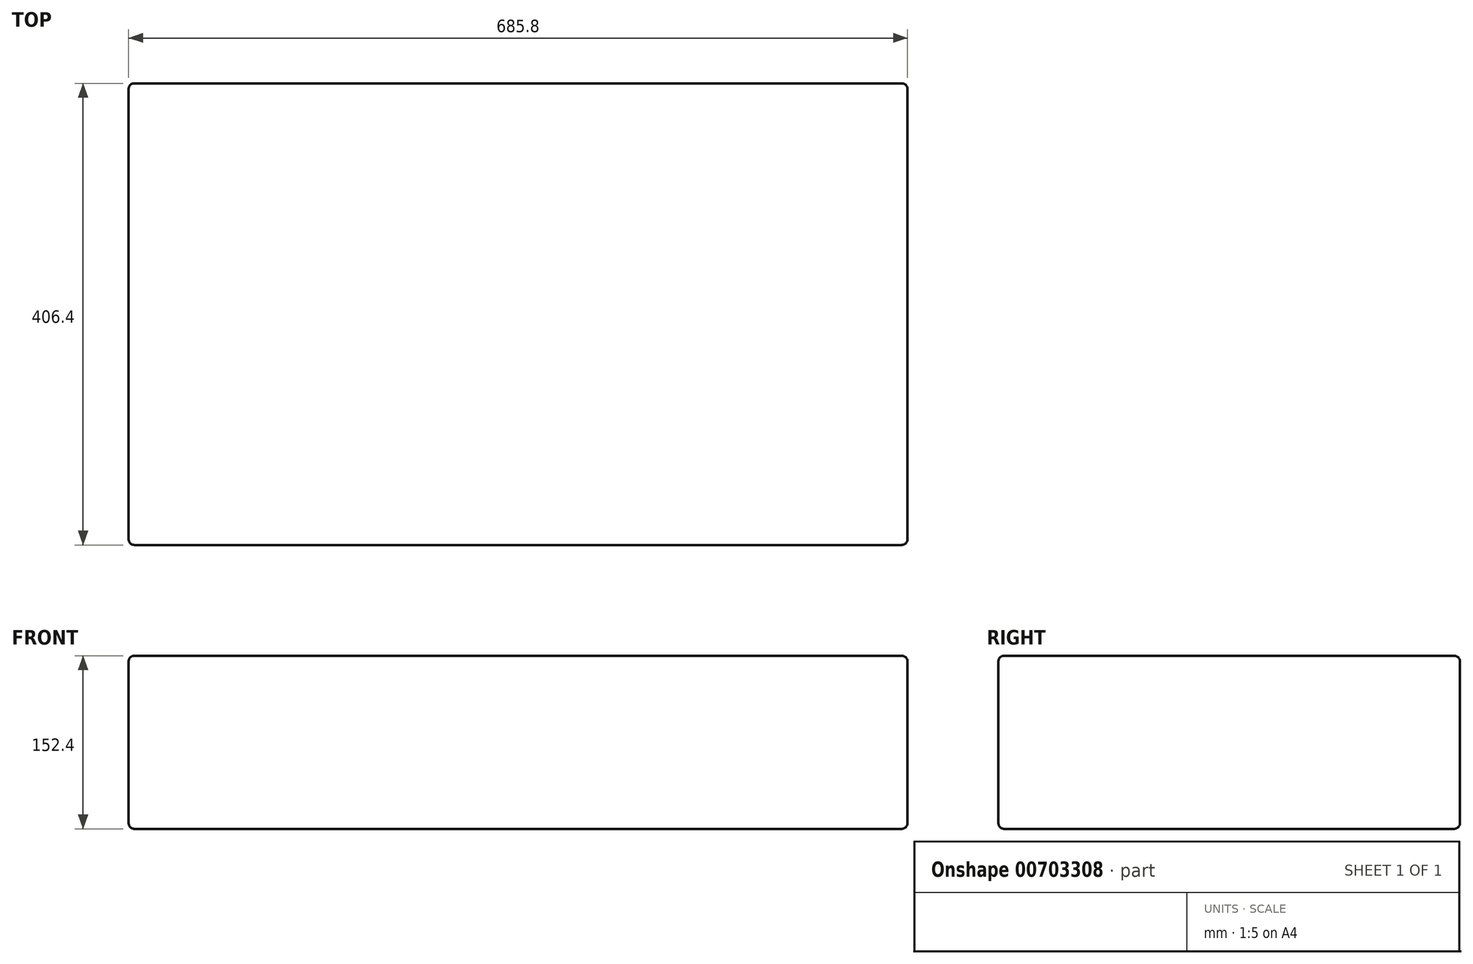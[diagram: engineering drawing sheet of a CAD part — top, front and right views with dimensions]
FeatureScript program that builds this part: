
annotation { "Feature Type Name" : "Feature", "Feature Type Description" : "" }
export const myFeature = defineFeature(function(context is Context, id is Id, definition is map)
    precondition{}
    {
        {
            var Q0;
            Q0=qCreatedBy(makeId("Top.planeOp"),FACE);
            var sketch = newSketch(context, id + "F0", { "sketchPlane" : qUnion([Q0])});
            skLineSegment(sketch, "E0", {"start": v(0, 0) * mm, "end": v(-342.9, 0) * mm, "construction": true});
            skLineSegment(sketch, "E1", {"start": v(0, 0) * mm, "end": v(342.9, 0) * mm, "construction": true});
            skLineSegment(sketch, "E2", {"start": v(0, 0) * mm, "end": v(0, 203.2) * mm, "construction": true});
            skLineSegment(sketch, "E3", {"start": v(0, 0) * mm, "end": v(0, -203.2) * mm, "construction": true});
            skLineSegment(sketch, "E4.bottom", {"start": v(-342.9, 203.2) * mm, "end": v(342.9, 203.2) * mm});
            skLineSegment(sketch, "E4.top", {"start": v(-342.9, -203.2) * mm, "end": v(342.9, -203.2) * mm});
            skLineSegment(sketch, "E4.left", {"start": v(-342.9, 203.2) * mm, "end": v(-342.9, -203.2) * mm});
            skLineSegment(sketch, "E4.right", {"start": v(342.9, 203.2) * mm, "end": v(342.9, -203.2) * mm});
            skSolve(sketch);
        }
        {
            var Q0;
            Q0=makeQuery(id+"F0.imprint","IMPRINT",FACE,{"disambiguationData":[TD([[makeQuery(id+"F0.imprint","IMPRINT",EDGE,{"derivedFrom":sQuery(id+"F0.wireOp",EDGE,"E4.bottom")}),-1.0]])]});
            extrude(context, id + "F1", {"entities" : qUnion([Q0]), "depth" : 152.4 * mm, "offsetDistance" : 25.4 * mm});
        }
        {
            var Q0;
            Q0=makeQuery(id+"F1.opExtrude","CAP_EDGE",EDGE,{"disambiguationData":[OSD([sQuery(id+"F0.wireOp",EDGE,"E4.top")])],"isStart":true});
            var Q1;
            Q1=makeQuery(id+"F1.opExtrude","CAP_EDGE",EDGE,{"disambiguationData":[OSD([sQuery(id+"F0.wireOp",EDGE,"E4.top")])],"isStart":false});
            var Q2;
            Q2=makeQuery(id+"F1.opExtrude","CAP_EDGE",EDGE,{"disambiguationData":[OSD([sQuery(id+"F0.wireOp",EDGE,"E4.bottom")])],"isStart":false});
            var Q3;
            Q3=makeQuery(id+"F1.opExtrude","CAP_EDGE",EDGE,{"disambiguationData":[OSD([sQuery(id+"F0.wireOp",EDGE,"E4.left")])],"isStart":false});
            var Q4;
            Q4=makeQuery(id+"F1.opExtrude","SWEPT_EDGE",EDGE,{"disambiguationData":[OSD([sQuery(id+"F0.wireOp",EDGE,"E4.top"),sQuery(id+"F0.wireOp",EDGE,"E4.right")])]});
            var Q5;
            Q5=makeQuery(id+"F1.opExtrude","SWEPT_EDGE",EDGE,{"disambiguationData":[OSD([sQuery(id+"F0.wireOp",EDGE,"E4.top"),sQuery(id+"F0.wireOp",EDGE,"E4.left")])]});
            var Q6;
            Q6=makeQuery(id+"F1.opExtrude","SWEPT_EDGE",EDGE,{"disambiguationData":[OSD([sQuery(id+"F0.wireOp",EDGE,"E4.bottom"),sQuery(id+"F0.wireOp",EDGE,"E4.right")])]});
            var Q7;
            Q7=makeQuery(id+"F1.opExtrude","CAP_EDGE",EDGE,{"disambiguationData":[OSD([sQuery(id+"F0.wireOp",EDGE,"E4.right")])],"isStart":true});
            var Q8;
            Q8=makeQuery(id+"F1.opExtrude","CAP_EDGE",EDGE,{"disambiguationData":[OSD([sQuery(id+"F0.wireOp",EDGE,"E4.right")])],"isStart":false});
            var Q9;
            Q9=makeQuery(id+"F1.opExtrude","CAP_EDGE",EDGE,{"disambiguationData":[OSD([sQuery(id+"F0.wireOp",EDGE,"E4.left")])],"isStart":true});
            var Q10;
            Q10=makeQuery(id+"F1.opExtrude","CAP_EDGE",EDGE,{"disambiguationData":[OSD([sQuery(id+"F0.wireOp",EDGE,"E4.bottom")])],"isStart":true});
            var Q11;
            Q11=makeQuery(id+"F1.opExtrude","SWEPT_EDGE",EDGE,{"disambiguationData":[OSD([sQuery(id+"F0.wireOp",EDGE,"E4.bottom"),sQuery(id+"F0.wireOp",EDGE,"E4.left")])]});
            fillet(context, id + "F2", {"entities" : qUnion([Q0, Q1, Q2, Q3, Q4, Q5, Q6, Q7, Q8, Q9, Q10, Q11]), "radius" : 5.08 * mm, "tangentPropagation" : true, "allowEdgeOverflow" : false});
        }
    });
